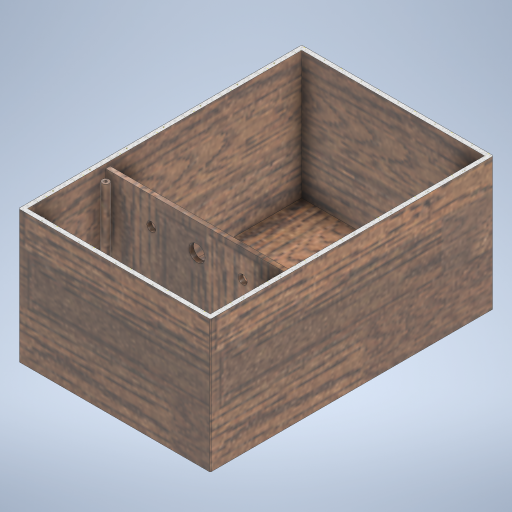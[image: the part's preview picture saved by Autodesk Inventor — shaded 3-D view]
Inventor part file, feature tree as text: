
AUTODESK INVENTOR PART (.ipt)
format: ipt  version: 2023.1 (Build 271208000, 208)  size: 539,648 bytes
history: native  units: in
note: dims shown in document units (in); Inventor stores cm internally (conversion verified against a paired STEP export)
features: extrude x5, sketch x5, other x1, shell x1, chamfer x1
ambient origin geometry x8: Origin, YZ Plane, XZ Plane, XY Plane, X Axis, Y Axis, Z Axis, Center Point
bodies: Body1 (feature_tree)
feature tree (13):
  other  "CrossSection1"
  extrude  "Extrusion3"  Depth=8.2677in
  shell  "Shell1"  Thickness=5.9055in
  extrude  "Extrusion4"  Depth=0.1969in
  sketch  "Sketch6"  dims[d14=0.0197in d15=0.0787in d16=-0.1969in d17=0.7874in]
  chamfer  "Chamfer1"  Distance=7.874in
  extrude  "Extrusion5"  Depth=1.1811in TaperAngle=45.0deg
  extrude  "Extrusion6"  Depth=0.3937in TaperAngle=0.0deg
  extrude  "Extrusion7"  Depth=1.1811in
  sketch  "Sketch4"  dims[d9=12.2047in d10=8.2677in d11=5.9055in]
  sketch  "Sketch5"  dims[d12=0.0in d13=0.1969in]
  sketch  "Sketch7"  dims[d18=0.1969in]
  sketch  "Sketch8"  dims[d19=5.315in d20=7.874in d21=0.0in d32=0.0394in d33=0.0787in d34=45.0deg d35=0.3937in d36=0.0in d37=0.315in d38=0.315in d39=0.315in d40=0.315in d41=0.2756in d42=0.2756in d43=0.2756in d44=0.2756in d45=0.2756in d46=0.2756in d47=0.2756in d48=0.2756in d49=5.1181in d50=0.0in d51=0.1181in d52=0.1181in d53=0.1181in d54=0.1181in d55=1.1811in d56=0.0in d4=0.5in d5=0.0344in d6=0.5in d7=0.0344in]
